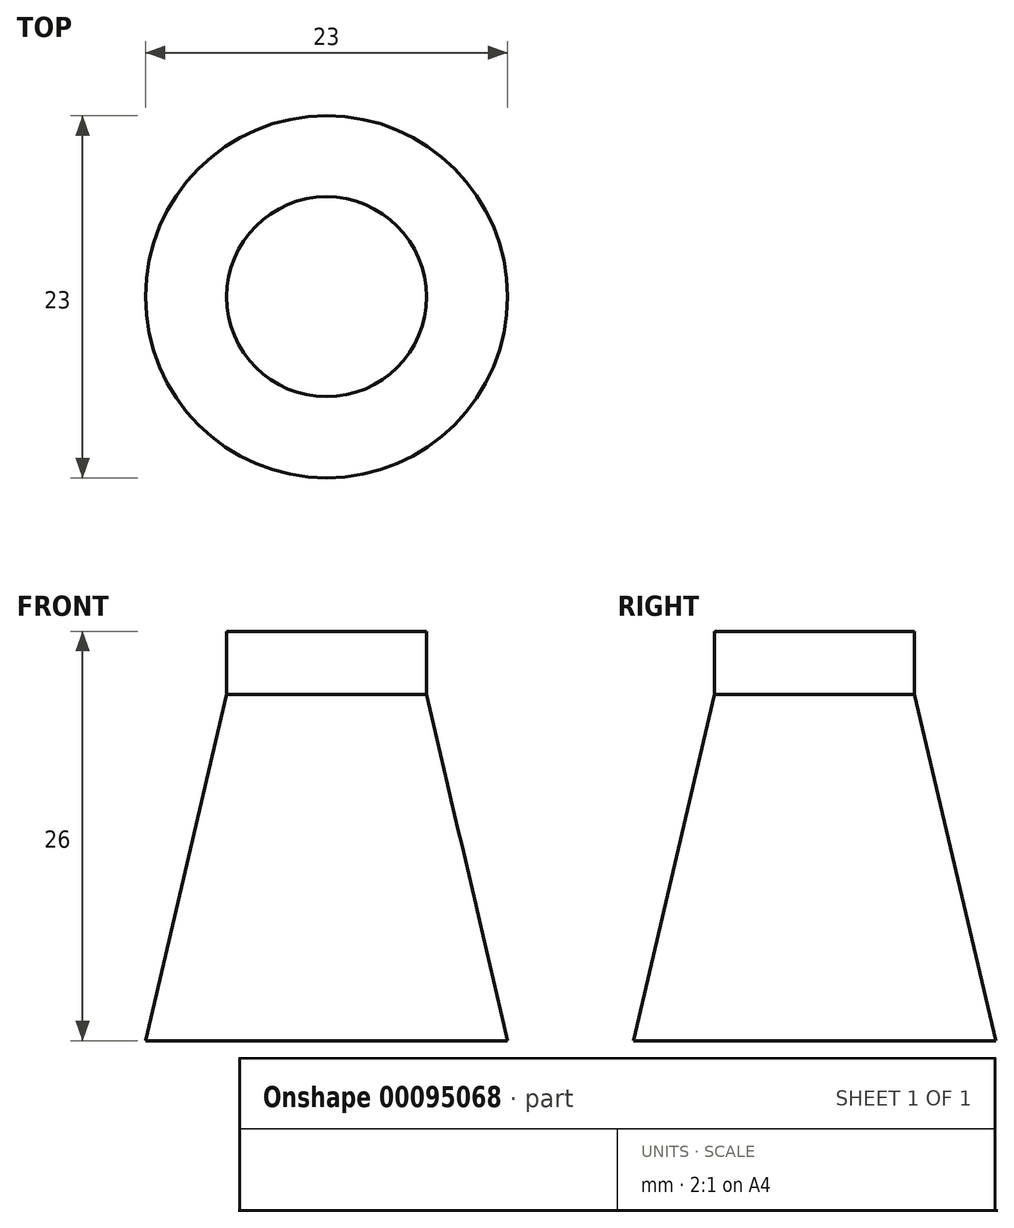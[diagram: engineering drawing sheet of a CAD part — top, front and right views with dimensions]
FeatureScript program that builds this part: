
annotation { "Feature Type Name" : "Feature", "Feature Type Description" : "" }
export const myFeature = defineFeature(function(context is Context, id is Id, definition is map)
    precondition{}
    {
        {
            var Q0;
            Q0=qCreatedBy(makeId("Right.planeOp"),FACE);
            var sketch = newSketch(context, id + "F0", { "sketchPlane" : qUnion([Q0])});
            skLineSegment(sketch, "E0", {"start": v(0, 0) * mm, "end": v(11.5, 0) * mm});
            skLineSegment(sketch, "E1", {"start": v(6.35, 22) * mm, "end": v(11.5, 0) * mm});
            skLineSegment(sketch, "E2", {"start": v(6.35, 22) * mm, "end": v(6.35, 26) * mm});
            skLineSegment(sketch, "E3", {"start": v(6.35, 26) * mm, "end": v(0, 26) * mm});
            skLineSegment(sketch, "E4", {"start": v(0, 26) * mm, "end": v(0, 0) * mm});
            skSolve(sketch);
        }
        {
            var Q0;
            Q0 = qSketchRegion(id + "F0", true);
            var Q1;
            Q1=sQuery(id+"F0.wireOp",EDGE,"E4");
            revolve(context, id + "F1", {"entities" : qUnion([Q0]), "axis" : qUnion([Q1]), "revolveType" : RevolveType.FULL});
        }
    });
